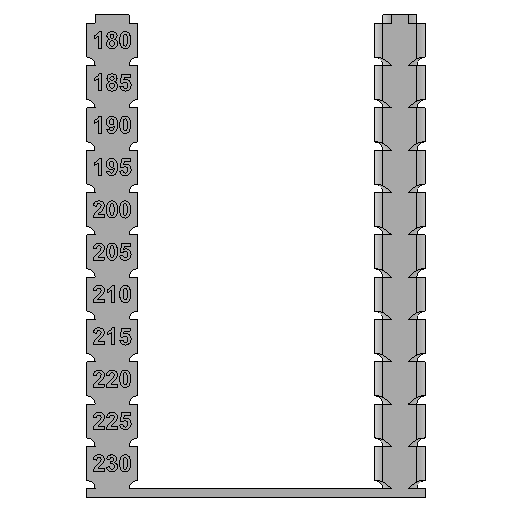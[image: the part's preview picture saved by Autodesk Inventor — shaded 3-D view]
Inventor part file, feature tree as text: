
AUTODESK INVENTOR PART (.ipt)
format: ipt  version: 2025.3 (Build 293356000, 356)  size: 1,722,880 bytes
history: native  units: mm
features: other x8, extrude x4, sketch x2, mirror x2, fillet x2, pattern_linear x2
ambient origin geometry x8: Origin, YZ Plane, XZ Plane, XY Plane, X Axis, Y Axis, Z Axis, Center Point
bodies: Body1 (feature_tree)
feature tree (20):
  other  "實體1"
  other  "temp_tower"
  sketch  "草圖1"
  extrude  "擠出1"  Depth=40.0mm
  extrude  "擠出2"  Depth=5.0mm
  mirror  "鏡射1"
  extrude  "擠出3"  Depth=6.0mm
  extrude  "擠出4"  Depth=1.0mm
  mirror  "鏡射2"
  fillet  "圓角1"  Radius=1.0mm
  pattern_linear  "矩形陣列1"  Spacing1=4.0mm  [1 undecoded]
  other  "合併1"
  fillet  "圓角2"  Radius=1.0mm
  pattern_linear  "矩形陣列2"  Spacing1=1.0mm  [1 undecoded]
  other  "浮雕1"
  other  "實體2"
  other  "陣列 實體2:1"
  other  "實體3"
  sketch  "草圖2"
  other  "MeshFeature1"
note: 2 required parameter values undecoded (feature->parameter linkage not recoverable at this tier; creation-order binding heuristic only, values carry confidence <= 0.55)
